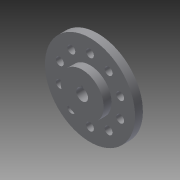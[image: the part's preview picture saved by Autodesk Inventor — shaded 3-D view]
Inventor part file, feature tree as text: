
AUTODESK INVENTOR PART (.ipt)
format: ipt  version: 2015 (Build 190159000, 159)  size: 134,656 bytes
history: native  units: in
note: dims shown in document units (in); Inventor stores cm internally (conversion verified against a paired STEP export)
features: sketch x3, hole x2, revolve x1, extrude x1, projected_geometry x1
ambient origin geometry x8: Origin, YZ Plane, XZ Plane, XY Plane, X Axis, Y Axis, Z Axis, Center Point
bodies: Solid1 (feature_tree)
feature tree (8):
  revolve  "Revolution1"  [1 undecoded]
  sketch  "Sketch2"  dims[d2=0.5in d3=1.0in]
  hole  "Hole1"  [1 undecoded]
  hole  "Hole2"  [1 undecoded]
  extrude  "Extrusion1"  Depth=0.125in
  sketch  "Sketch1"  dims[d0=1.0in d1=2.5in]
  projected_geometry  "Projected Loop1"
  sketch  "Sketch3"  dims[d4=0.375in d5=90.0deg d7=1.65in d8=0.5in d9=0.75in d10=0.375in d11=0.25in d12=0.5635in d13=1.0in d14=0.8108in d15=3.937in d17=360.0deg d19=0.5in d20=0.75in d21=0.375in d22=0.25in d23=0.5635in d24=1.0in d25=0.8108in d26=0.125in d27=0.125in d29=0.0625in d30=1.9259in d31=0.0in d33=1.6659in d34=0.0in d35=2.0in d36=0.0in]
note: 3 required parameter values undecoded (feature->parameter linkage not recoverable at this tier; creation-order binding heuristic only, values carry confidence <= 0.55)